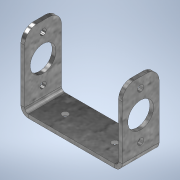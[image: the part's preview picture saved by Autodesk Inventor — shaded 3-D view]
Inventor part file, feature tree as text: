
AUTODESK INVENTOR PART (.ipt)
format: ipt  version: 2022 (Build 260153000, 153)  size: 205,824 bytes
history: native  units: in
note: dims shown in document units (in); Inventor stores cm internally (conversion verified against a paired STEP export)
features: sheet_metal_op x4, sketch x4, hole x3, other x2, projected_geometry x2, fillet x1
ambient origin geometry x8: Origin, YZ Plane, XZ Plane, XY Plane, X Axis, Y Axis, Z Axis, Center Point
bodies: Body1 (feature_tree)
feature tree (16):
  sheet_metal_op  "Face1"
  sheet_metal_op  "Flange1"
  sketch  "Sketch5"  dims[d14=0.16in d15=0.08in]
  hole  "Hole1"  [1 undecoded]
  hole  "Hole2"  [1 undecoded]
  fillet  "Fillet1"  Radius=0.04in
  hole  "Hole3"  [1 undecoded]
  sketch  "Sketch3"  dims[d9=2.1654in d10=0.7874in]
  other  "Plate1"
  sketch  "Sketch4"  dims[d11=0.08in d12=0.08in d13=0.04in]
  other  "Plate2"
  sheet_metal_op  "Bend1"
  sheet_metal_op  "Corner1"
  projected_geometry  "Projected Loop3"
  sketch  "Sketch6"  dims[d16=1.5748in d17=90.0deg d18=0.08in d19=0.32in d20=0.08in d21=0.08in d22=0.4921in d23=0.4921in d24=0.1339in d25=0.2362in d26=0.2559in d27=0.1181in d28=0.6181in d29=0.08in d30=0.8108in d31=0.5512in d32=0.2362in d33=0.1575in d34=0.0787in d35=90.0deg d36=0.315in d37=0.8108in d38=0.2662in d39=0.3937in d40=0.1339in d41=0.2362in d42=0.2559in d43=0.1181in d44=90.0deg d45=0.315in d46=0.8108in d7=0.0197in d8=1.9685in]
  projected_geometry  "Projected Loop4"
note: 3 required parameter values undecoded (feature->parameter linkage not recoverable at this tier; creation-order binding heuristic only, values carry confidence <= 0.55)
